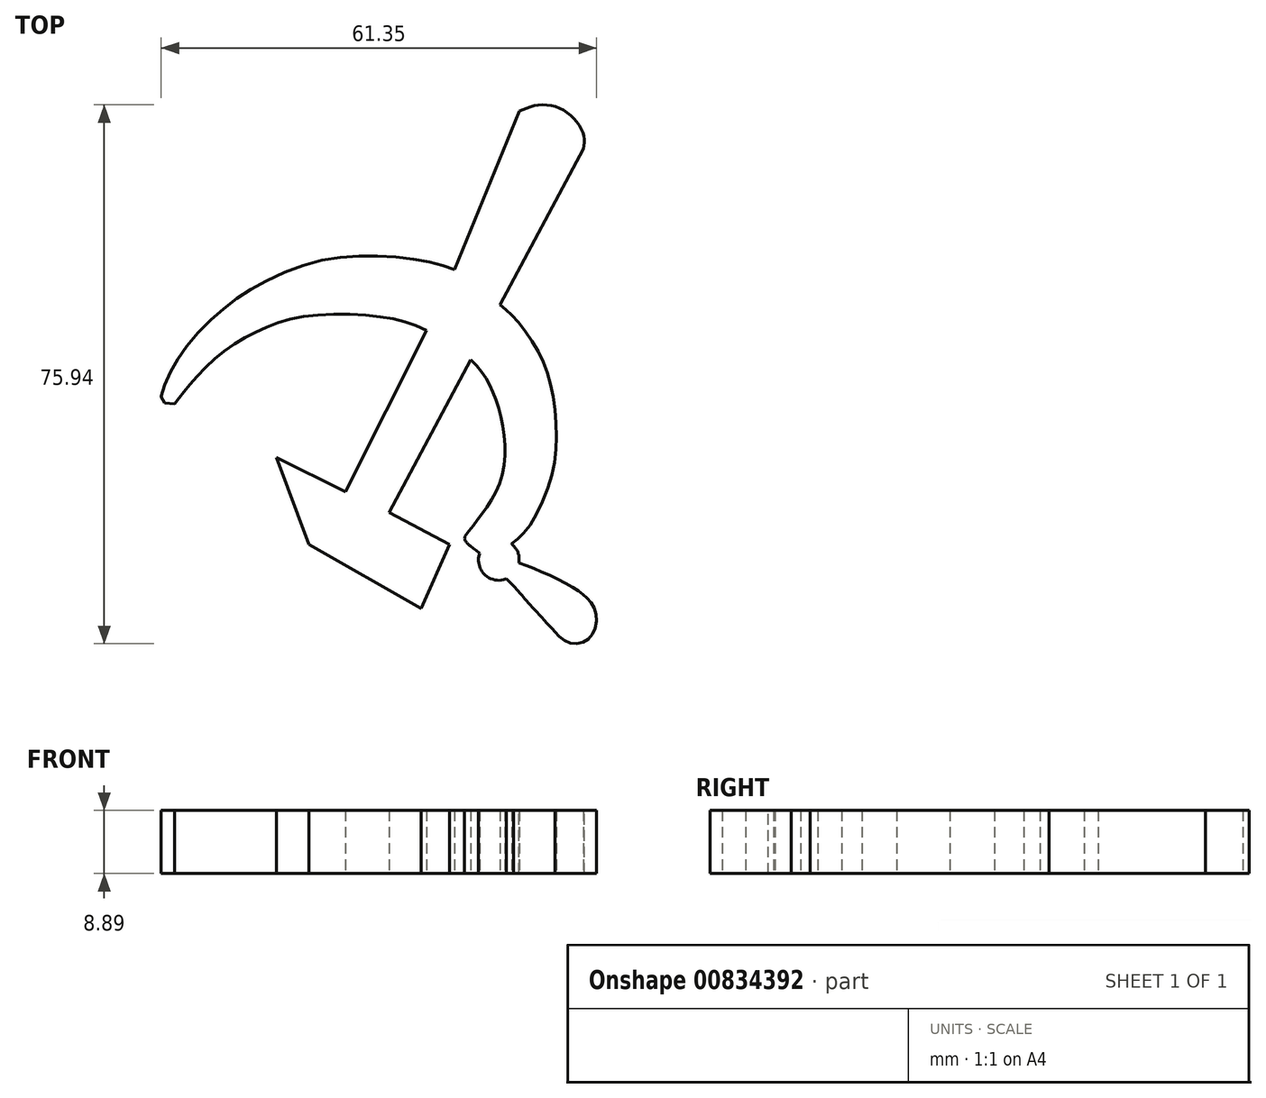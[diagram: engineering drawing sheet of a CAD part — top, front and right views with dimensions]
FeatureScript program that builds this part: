
annotation { "Feature Type Name" : "Feature", "Feature Type Description" : "" }
export const myFeature = defineFeature(function(context is Context, id is Id, definition is map)
    precondition{}
    {
        {
            var Q0;
            Q0=qCreatedBy(makeId("Top.planeOp"),FACE);
            var sketch = newSketch(context, id + "F0", { "sketchPlane" : qUnion([Q0])});
            skLineSegment(sketch, "E0", {"start": v(30.25, -23.08) * mm, "end": v(57.58, 28.18) * mm});
            skLineSegment(sketch, "E1", {"start": v(24.06, -20.2) * mm, "end": v(35.47, 2.59) * mm});
            skLineSegment(sketch, "E2", {"start": v(39.43, 11.11) * mm, "end": v(48.6, 33.48) * mm});
            skFitSpline(sketch, "E3", {"points": [v(0, -7.8) * mm, v(1.77, -5.54) * mm, v(6.02, -1.1) * mm, v(11.73, 2.49) * mm, v(18.67, 4.6) * mm, v(29.36, 4.45) * mm, v(35.47, 2.59) * mm, v(41.72, -1.56) * mm, v(44.53, -5.38) * mm, v(46.24, -10.94) * mm, v(46.05, -18.16) * mm, v(43.26, -23.35) * mm, v(40.91, -26.46) * mm], "startDerivative": vector(27.44, 36.2) * mm, "endDerivative": vector(-33.94, -43.82) * mm});
            skFitSpline(sketch, "E4", {"points": [v(47.5, -27.49) * mm, v(49.51, -25.63) * mm, v(52.74, -19.19) * mm, v(53.77, -12.3) * mm, v(53.02, -5.18) * mm, v(51, 0) * mm, v(47.8, 4.41) * mm, v(45.84, 6.16) * mm], "startDerivative": vector(18.9, 13.8) * mm, "endDerivative": vector(-18.38, 14.53) * mm});
            skFitSpline(sketch, "E5", {"points": [v(39.43, 11.11) * mm, v(35.47, 12.33) * mm, v(28.1, 13.04) * mm, v(20.13, 12.31) * mm, v(11.81, 8.97) * mm, v(6.42, 5.17) * mm, v(1.43, 0) * mm, v(-1.15, -4.56) * mm, v(-1.78, -7.32) * mm, v(0, -7.8) * mm], "startDerivative": vector(-37.55, 13.86) * mm, "endDerivative": vector(35.64, -1.47) * mm});
            skFitSpline(sketch, "E6", {"points": [v(39.43, 11.11) * mm, v(42.23, 9.73) * mm, v(45.84, 6.16) * mm], "startDerivative": vector(6.37, -2.44) * mm, "endDerivative": vector(6.46, -7.27) * mm});
            skFitSpline(sketch, "E7", {"points": [v(48.6, 33.48) * mm, v(50.94, 34.29) * mm, v(54.02, 33.98) * mm, v(56.5, 32.14) * mm, v(57.7, 29.84) * mm, v(57.58, 28.18) * mm], "startDerivative": vector(11.2, 5.1) * mm, "endDerivative": vector(-2.17, -9.92) * mm});
            skLineSegment(sketch, "E8", {"start": v(30.25, -23.08) * mm, "end": v(38.72, -27.6) * mm});
            skLineSegment(sketch, "E9", {"start": v(38.72, -27.6) * mm, "end": v(34.76, -36.6) * mm});
            skLineSegment(sketch, "E10", {"start": v(34.76, -36.6) * mm, "end": v(18.93, -27.6) * mm});
            skLineSegment(sketch, "E11", {"start": v(18.93, -27.6) * mm, "end": v(14.33, -15.32) * mm});
            skLineSegment(sketch, "E12", {"start": v(14.33, -15.32) * mm, "end": v(24.06, -20.2) * mm});
            skFitSpline(sketch, "E13", {"points": [v(40.91, -26.46) * mm, v(40.91, -26.98) * mm, v(43.12, -28.94) * mm], "startDerivative": vector(-0.46, -1.6) * mm, "endDerivative": vector(4.24, -3.15) * mm});
            skFitSpline(sketch, "E14", {"points": [v(47.5, -27.49) * mm, v(47.6, -27.64) * mm, v(48.06, -28.16) * mm, v(48.48, -29.08) * mm, v(48.53, -30.18) * mm], "startDerivative": vector(0.58, -1.05) * mm, "endDerivative": vector(-0.08, -3.52) * mm});
            skFitSpline(sketch, "E15", {"points": [v(42.98, -28.83) * mm, v(42.89, -29.16) * mm, v(42.82, -29.78) * mm, v(42.91, -30.5) * mm, v(43.08, -30.96) * mm, v(43.28, -31.33) * mm, v(43.83, -31.96) * mm, v(44.42, -32.35) * mm, v(45.14, -32.6) * mm, v(45.85, -32.64) * mm, v(46.48, -32.54) * mm, v(46.74, -32.45) * mm], "startDerivative": vector(-1.32, -4.28) * mm, "endDerivative": vector(3.63, 1.41) * mm});
            skFitSpline(sketch, "E16", {"points": [v(46.74, -32.45) * mm, v(47.77, -33.41) * mm, v(49.9, -35.45) * mm, v(52.66, -38.58) * mm, v(54.49, -40.85) * mm, v(56.91, -41.56) * mm, v(58.9, -40.2) * mm, v(59.38, -37.33) * mm, v(58.17, -35.2) * mm, v(56.49, -33.87) * mm, v(52.48, -31.77) * mm, v(48.53, -30.18) * mm], "startDerivative": vector(14.91, -14) * mm, "endDerivative": vector(-34.88, 13.17) * mm});
            skFitSpline(sketch, "E17", {"points": [v(47.77, -33.41) * mm, v(48.38, -34.14) * mm, v(49.74, -35.7) * mm, v(53.58, -39.88) * mm], "startDerivative": vector(2.82, -3.35) * mm, "endDerivative": vector(8.67, -9.3) * mm});
            skSolve(sketch);
        }
        {
            var Q0;
            Q0 = qSketchRegion(id + "F0", true);
            extrude(context, id + "F1", {"entities" : qUnion([Q0]), "depth" : 8.9 * mm, "offsetDistance" : 25.4 * mm});
        }
    });
